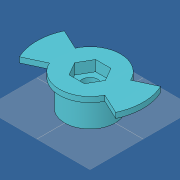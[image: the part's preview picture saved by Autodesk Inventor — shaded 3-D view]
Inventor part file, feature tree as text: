
AUTODESK INVENTOR PART (.ipt)
format: ipt  version: 2019 (Build 230136000, 136)  size: 120,320 bytes
history: native  units: mm
features: extrude x3, sketch x2
ambient origin geometry x8: Origin, YZ Plane, XZ Plane, XY Plane, X Axis, Y Axis, Z Axis, Center Point
bodies: Volumenkörper1 (feature_tree)
feature tree (5):
  sketch  "Skizze1"  dims[d0=19.0mm d1=23.0mm]
  extrude  "Extrusion1"  Depth=23.0mm
  extrude  "Extrusion2"  Depth=4.0mm
  extrude  "Extrusion3"  Depth=2.0mm TaperAngle=0.0deg
  sketch  "Skizze2"  dims[d2=17.0mm d3=6.0mm d4=2.0mm d5=0.0mm d6=10.0mm d7=0.0mm d8=40.0mm d10=8.726646mm d11=10.0mm d12=4.0mm d13=0.0mm]
